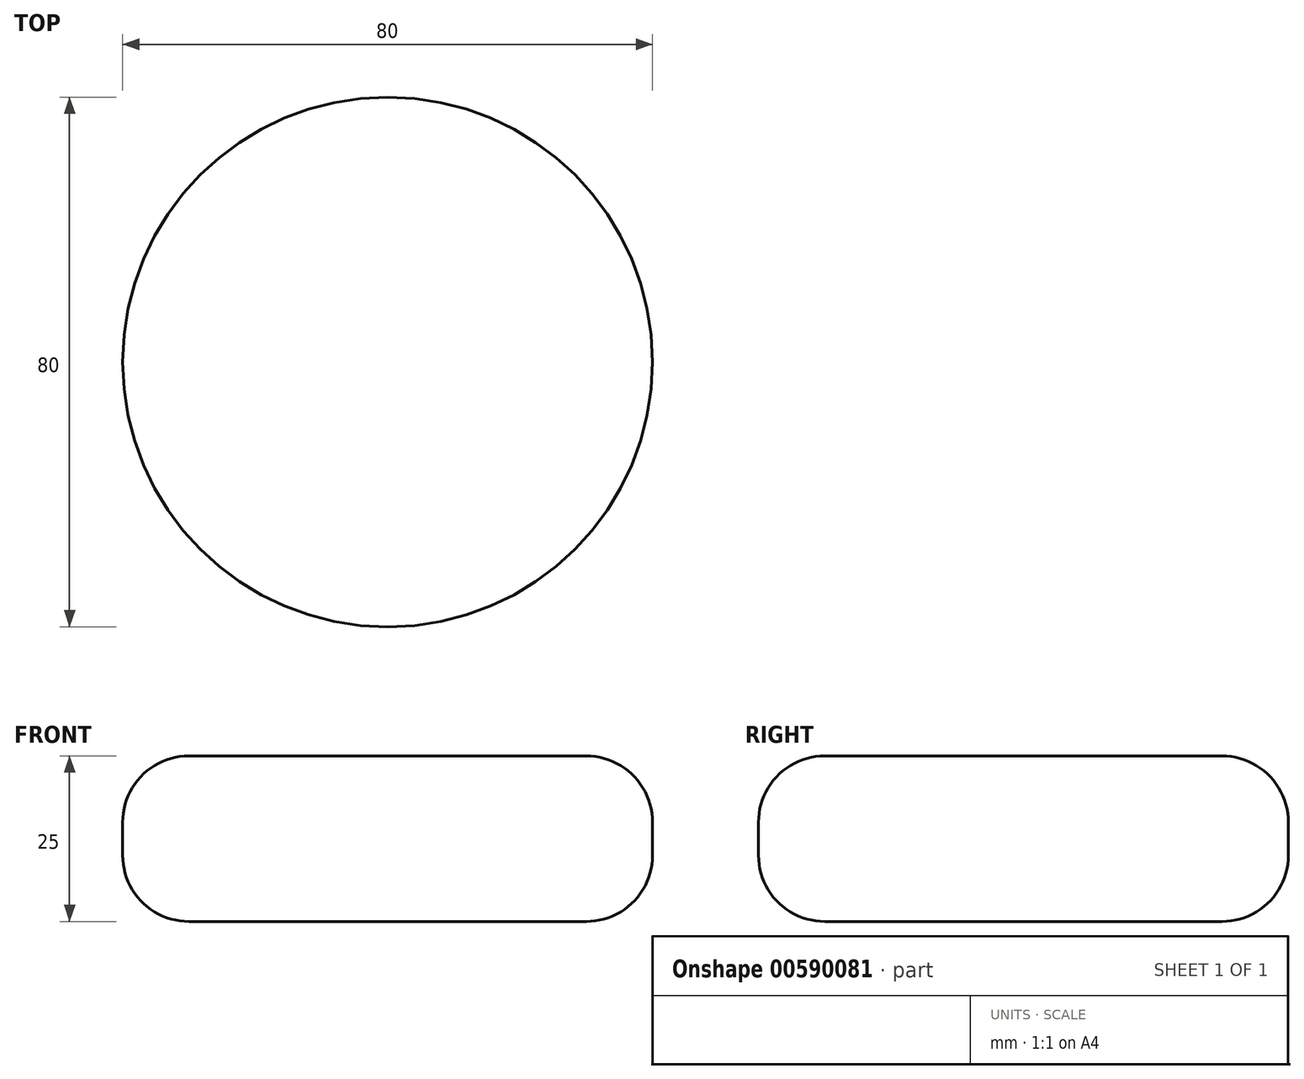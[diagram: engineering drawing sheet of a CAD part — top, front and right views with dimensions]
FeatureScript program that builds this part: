
annotation { "Feature Type Name" : "Feature", "Feature Type Description" : "" }
export const myFeature = defineFeature(function(context is Context, id is Id, definition is map)
    precondition{}
    {
        {
            var Q0;
            Q0=qCreatedBy(makeId("Top.planeOp"),FACE);
            var sketch = newSketch(context, id + "F0", { "sketchPlane" : qUnion([Q0])});
            skCircle(sketch, "E0", {"center": v(0, 0) * mm, "radius": 40 * mm});
            skSolve(sketch);
        }
        {
            var Q0;
            Q0=makeQuery(id+"F0.imprint","IMPRINT",FACE,{"disambiguationData":[TD([[makeQuery(id+"F0.imprint","IMPRINT",EDGE,{"derivedFrom":sQuery(id+"F0.wireOp",EDGE,"E0")}),1.0]])]});
            extrude(context, id + "F1", {"entities" : qUnion([Q0]), "depth" : 25 * mm, "offsetDistance" : 25 * mm});
        }
        {
            var Q0;
            Q0=makeQuery(id+"F1.opExtrude","CAP_FACE",FACE,{"disambiguationData":[OSD([sQuery(id+"F0.wireOp",EDGE,"E0")])],"isStart":false});
            var Q1;
            Q1=makeQuery(id+"F1.opExtrude","CAP_FACE",FACE,{"disambiguationData":[OSD([sQuery(id+"F0.wireOp",EDGE,"E0")])],"isStart":true});
            fillet(context, id + "F2", {"entities" : qUnion([Q0, Q1]), "radius" : 10 * mm, "tangentPropagation" : true, "allowEdgeOverflow" : false});
        }
    });
